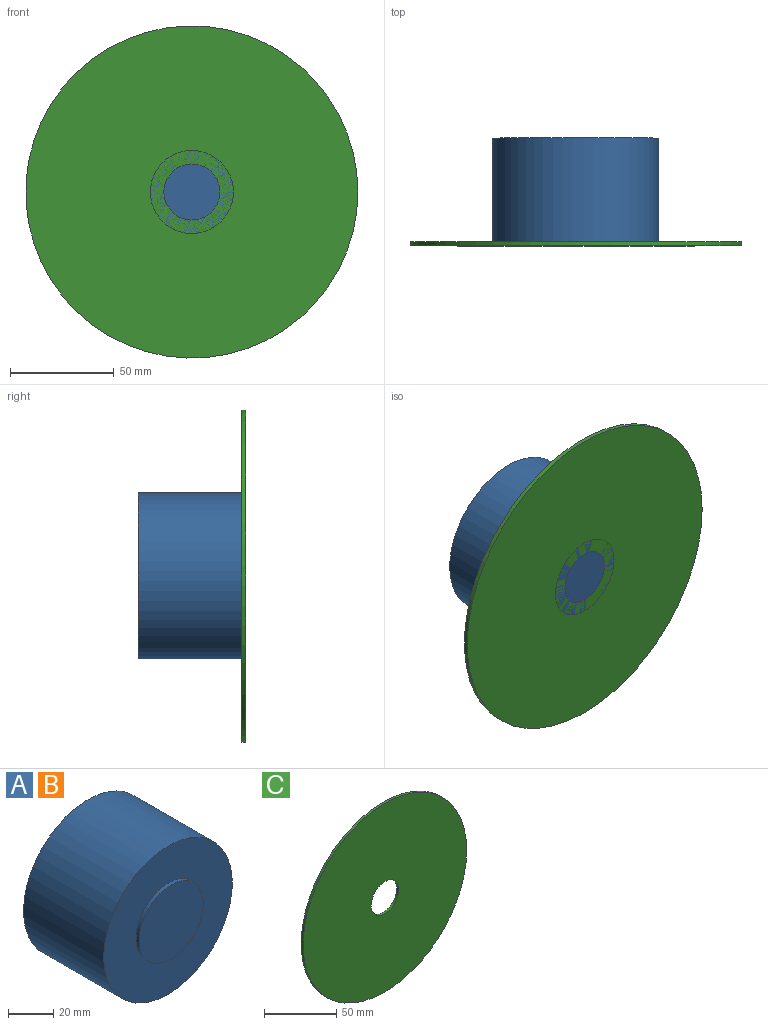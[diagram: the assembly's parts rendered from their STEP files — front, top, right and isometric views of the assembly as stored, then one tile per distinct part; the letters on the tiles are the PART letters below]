
ASSEMBLY  parts=3 mates=1
PART A: 5 faces, bbox 80x51.9x80 mm
  f0: cylinder r=40mm len=80mm, axis (0,1,0), area 12566.4mm2, adj f1,f2
  f1: plane 80x80mm, normal (0,-1,0), area 3769.9mm2, adj f0,f3
  f2: plane 80x80mm, normal (0,1,0), area 5026.5mm2, adj f0
  f3: cylinder r=20mm len=40mm, axis (0,1,0), area 238.8mm2, adj f1,f4
  f4: plane 40x40mm, normal (0,-1,0), area 1256.6mm2, adj f3
PART B: same geometry as A
PART C: 4 faces, bbox 160x1.9x160 mm
  f0: cylinder r=13.5mm len=27mm, axis (0,1,0), area 161.2mm2, adj f2,f3
  f1: cylinder r=80mm len=160mm, axis (0,1,0), area 955mm2, adj f2,f3
  f2: plane 160x160mm, normal (0,-1,0), area 19533.6mm2, adj f0,f1
  f3: plane 160x160mm, normal (0,1,0), area 19533.6mm2, adj f0,f1
PLACE A t=(37.89,68.18,30.53)mm
PLACE B t=(37.89,68.18,30.53)mm
PLACE C t=(37.89,18.18,30.53)mm
MATE fastened C.f0 <-> B.f0  axis (0,-1,0) through (37.89,16.28,30.53)mm
